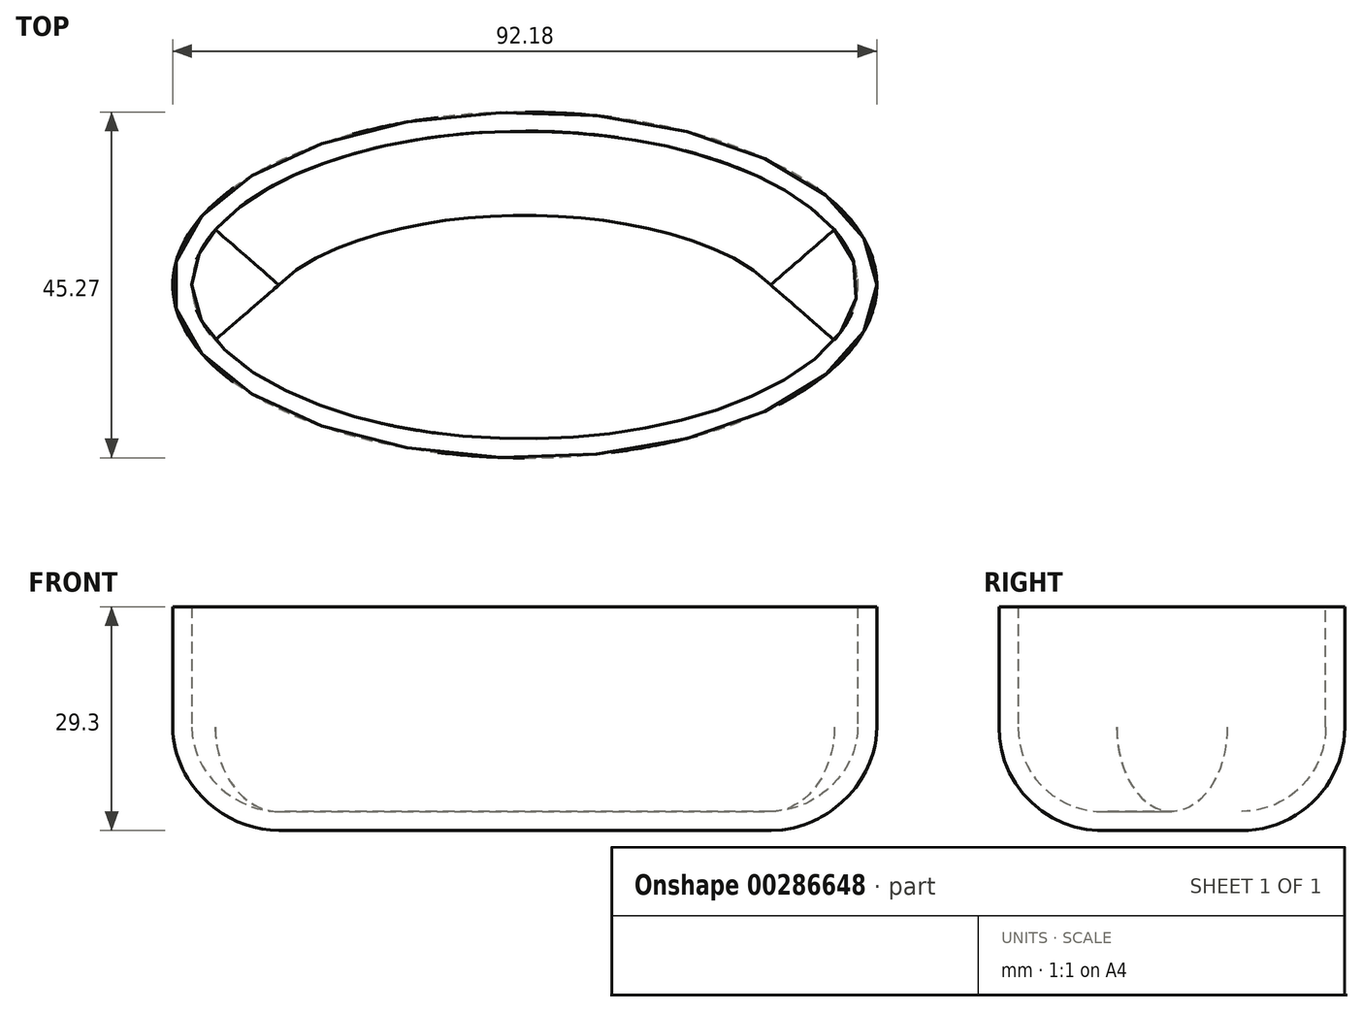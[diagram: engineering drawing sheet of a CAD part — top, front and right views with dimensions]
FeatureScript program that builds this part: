
annotation { "Feature Type Name" : "Feature", "Feature Type Description" : "" }
export const myFeature = defineFeature(function(context is Context, id is Id, definition is map)
    precondition{}
    {
        {
            var Q0;
            Q0=qCreatedBy(makeId("Top.planeOp"),FACE);
            var sketch = newSketch(context, id + "F0", { "sketchPlane" : qUnion([Q0])});
            skEllipse(sketch, "E0", {"center": v(-21.57, 18.47) * mm, "majorRadius": 46.09 * mm, "minorRadius": 22.63 * mm, "majorAxis": v(1, 0)});
            skSolve(sketch);
        }
        {
            var Q0;
            Q0=makeQuery(id+"F0.imprint","IMPRINT",FACE,{"disambiguationData":[TD([[makeQuery(id+"F0.imprint","IMPRINT",EDGE,{"derivedFrom":sQuery(id+"F0.wireOp",EDGE,"E0")}),1.0]])]});
            extrude(context, id + "F1", {"entities" : qUnion([Q0]), "depth" : 29.3 * mm});
        }
        {
            var Q0;
            Q0=makeQuery(id+"F1.opExtrude","CAP_EDGE",EDGE,{"disambiguationData":[OSD([sQuery(id+"F0.wireOp",EDGE,"E0")])],"isStart":true});
            fillet(context, id + "F2", {"entities" : qUnion([Q0]), "radius" : 13.52 * mm, "tangentPropagation" : true, "allowEdgeOverflow" : false});
        }
        {
            var Q0;
            Q0=makeQuery(id+"F1.opExtrude","CAP_FACE",FACE,{"disambiguationData":[OSD([sQuery(id+"F0.wireOp",EDGE,"E0")])],"isStart":false});
            shell(context, id + "F3", {"entities" : qUnion([Q0]), "thickness" : 2.5 * mm});
        }
    });
